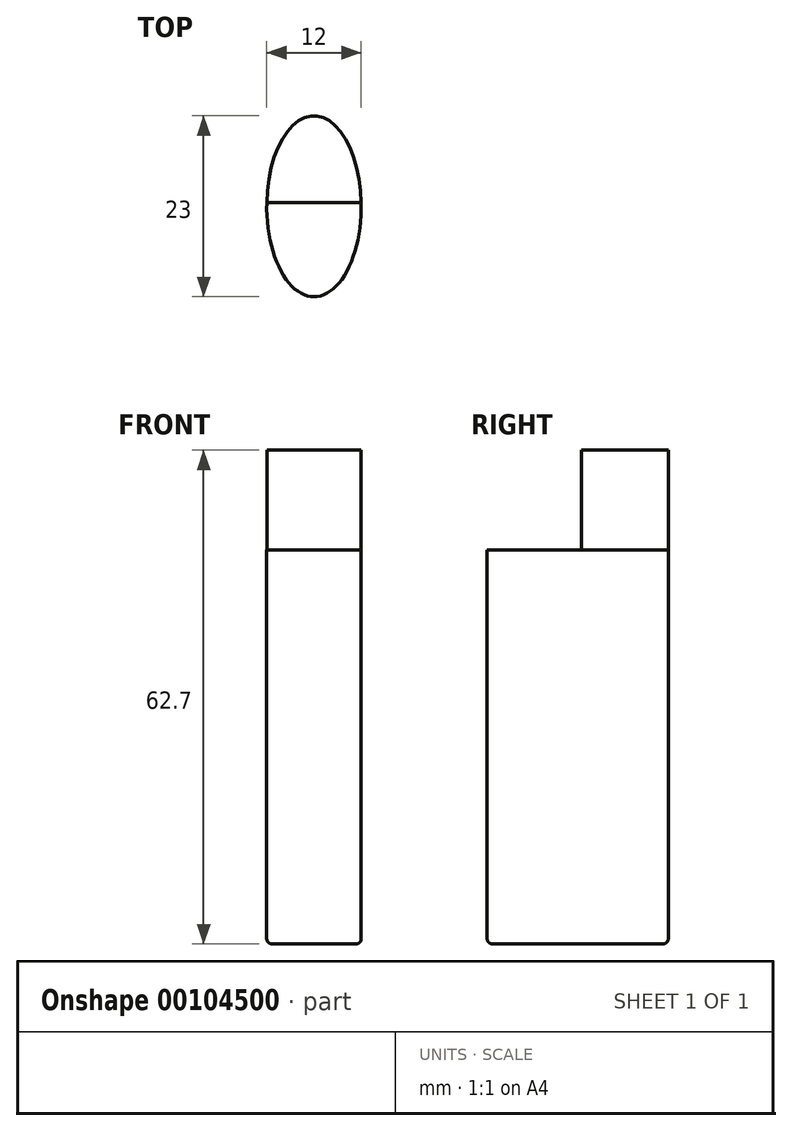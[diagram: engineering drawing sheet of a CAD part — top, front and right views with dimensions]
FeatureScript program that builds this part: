
annotation { "Feature Type Name" : "Feature", "Feature Type Description" : "" }
export const myFeature = defineFeature(function(context is Context, id is Id, definition is map)
    precondition{}
    {
        {
            var Q0;
            Q0=qCreatedBy(makeId("Top.planeOp"),FACE);
            var sketch = newSketch(context, id + "F0", { "sketchPlane" : qUnion([Q0])});
            skEllipse(sketch, "E0", {"center": v(0, 0) * mm, "majorRadius": 11.5 * mm, "minorRadius": 6 * mm, "majorAxis": v(0, -1)});
            skSolve(sketch);
        }
        {
            var Q0;
            Q0=makeQuery(id+"F0.imprint","IMPRINT",FACE,{"disambiguationData":[TD([[makeQuery(id+"F0.imprint","IMPRINT",EDGE,{"derivedFrom":sQuery(id+"F0.wireOp",EDGE,"E0")}),1.0]])]});
            extrude(context, id + "F1", {"entities" : qUnion([Q0]), "depth" : 50 * mm});
        }
        {
            var Q0;
            Q0=makeQuery(id+"F1.opExtrude","CAP_EDGE",EDGE,{"disambiguationData":[OSD([sQuery(id+"F0.wireOp",EDGE,"E0")])],"isStart":true});
            fillet(context, id + "F2", {"entities" : qUnion([Q0]), "radius" : 0.64 * mm, "tangentPropagation" : true, "allowEdgeOverflow" : false});
        }
        {
            var Q0;
            Q0=makeQuery(id+"F1.opExtrude","CAP_FACE",FACE,{"disambiguationData":[OSD([sQuery(id+"F0.wireOp",EDGE,"E0")])],"isStart":false});
            var sketch = newSketch(context, id + "F3", { "sketchPlane" : qUnion([Q0])});
            skEllipticalArc(sketch, "E1", {});
            skLineSegment(sketch, "E2", {"start": v(-6, 0.45) * mm, "end": v(6, 0.45) * mm});
            const initialGuessF3  = {"E1": [0, 0, 0, -1, 0.0115, 0.006, 1.6098235003299806, 4.673361806849606]};
            skSetInitialGuess(sketch, initialGuessF3);
            skSolve(sketch);
        }
        {
            var Q0;
            Q0 = qSketchRegion(id + "F3", true);
            extrude(context, id + "F4", {"entities" : qUnion([Q0]), "depth" : 12.7 * mm});
        }
    });
